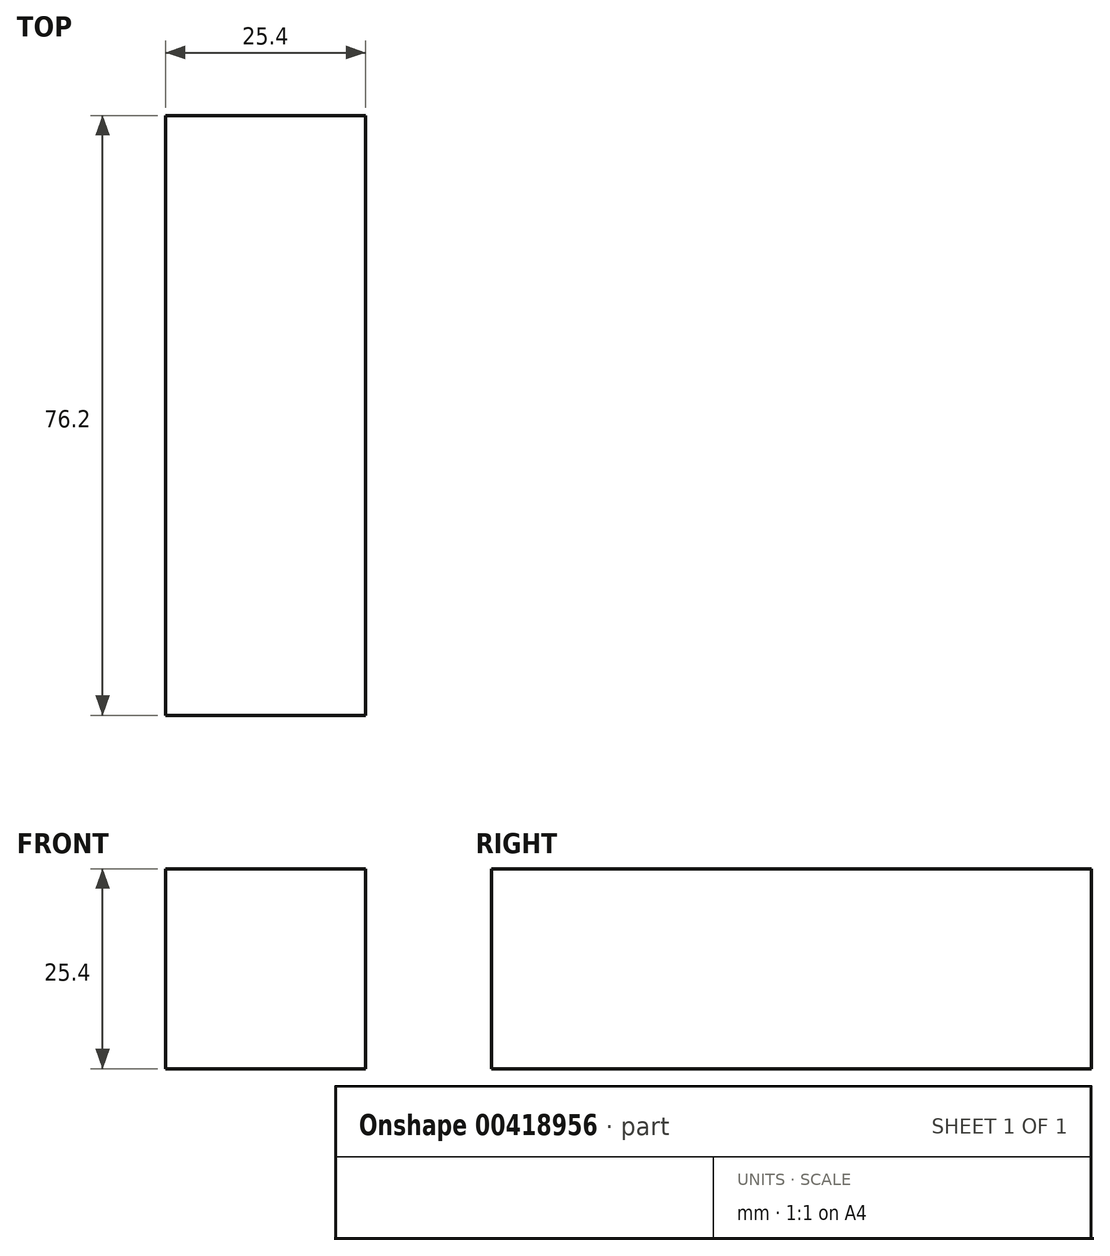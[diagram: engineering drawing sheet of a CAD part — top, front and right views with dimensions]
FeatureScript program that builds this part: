
annotation { "Feature Type Name" : "Feature", "Feature Type Description" : "" }
export const myFeature = defineFeature(function(context is Context, id is Id, definition is map)
    precondition{}
    {
        {
            var Q0;
            Q0=qCreatedBy(makeId("Front.planeOp"),FACE);
            var sketch = newSketch(context, id + "F0", { "sketchPlane" : qUnion([Q0])});
            skLineSegment(sketch, "E0.bottom", {"start": v(-50.42, 29.98) * mm, "end": v(-25.02, 29.98) * mm});
            skLineSegment(sketch, "E0.top", {"start": v(-50.42, 4.58) * mm, "end": v(-25.02, 4.58) * mm});
            skLineSegment(sketch, "E0.left", {"start": v(-50.42, 29.98) * mm, "end": v(-50.42, 4.58) * mm});
            skLineSegment(sketch, "E0.right", {"start": v(-25.02, 29.98) * mm, "end": v(-25.02, 4.58) * mm});
            skSolve(sketch);
        }
        {
            var Q0;
            Q0 = qSketchRegion(id + "F0", true);
            extrude(context, id + "F1", {"entities" : qUnion([Q0]), "depth" : 76.2 * mm});
        }
    });
